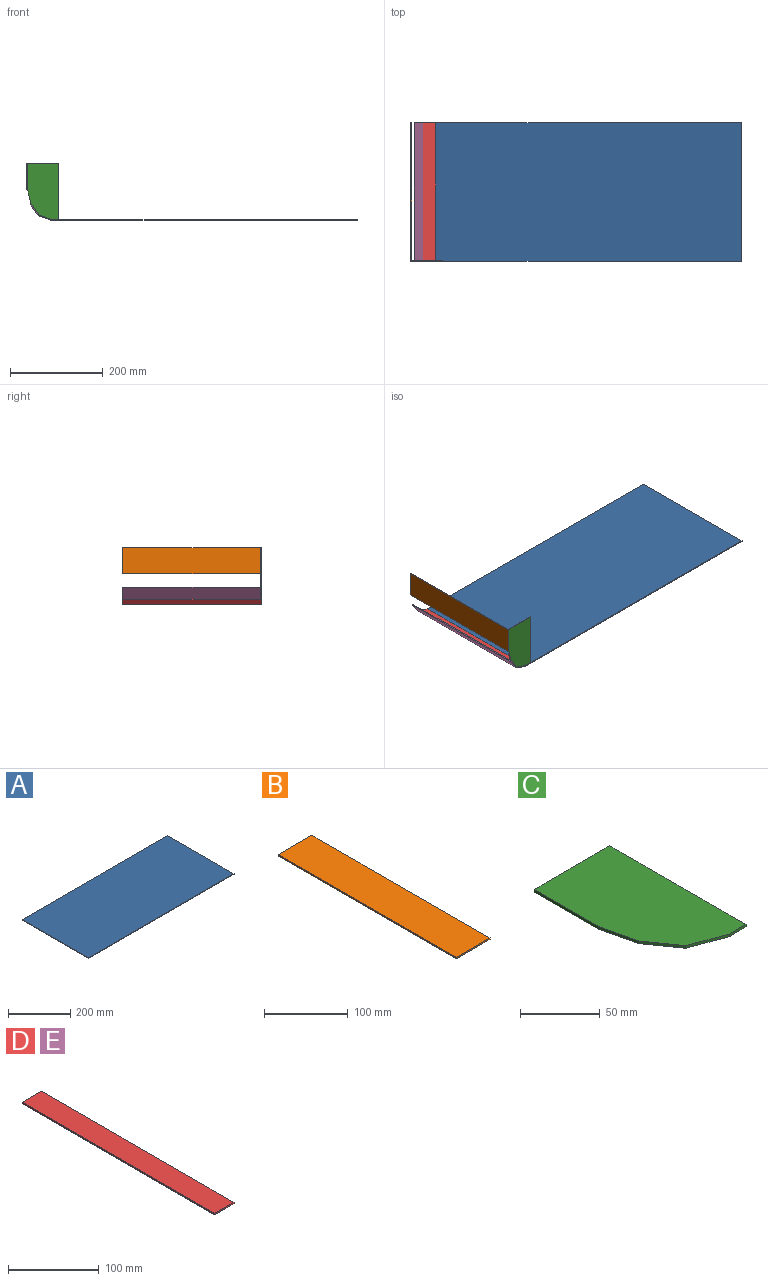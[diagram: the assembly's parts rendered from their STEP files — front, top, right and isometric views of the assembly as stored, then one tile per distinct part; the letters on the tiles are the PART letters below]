
ASSEMBLY  parts=5 mates=4
PART A: 6 faces, bbox 660x300x2 mm
  f0: plane 660x2mm, normal (0,1,0), area 1320mm2, adj f1,f3,f4,f5
  f1: plane 300x2mm, normal (-1,0,0), area 600mm2, adj f0,f2,f4,f5
  f2: plane 660x2mm, normal (0,-1,0), area 1320mm2, adj f1,f3,f4,f5
  f3: plane 300x2mm, normal (1,0,0), area 600mm2, adj f0,f2,f4,f5
  f4: plane 660x300mm, normal (0,0,-1), area 198000mm2, adj f0,f1,f2,f3
  f5: plane 660x300mm, normal (0,0,1), area 198000mm2, adj f0,f1,f2,f3
PART B: 6 faces, bbox 57x300x2 mm
  f0: plane 300x2mm, normal (-1,0,0), area 600mm2, adj f1,f3,f4,f5
  f1: plane 57x2mm, normal (0,-1,0), area 114mm2, adj f0,f2,f4,f5
  f2: plane 300x2mm, normal (1,0,0), area 600mm2, adj f1,f3,f4,f5
  f3: plane 57x2mm, normal (0,1,0), area 114mm2, adj f0,f2,f4,f5
  f4: plane 300x57mm, normal (0,0,-1), area 17100mm2, adj f0,f1,f2,f3
  f5: plane 300x57mm, normal (0,0,1), area 17100mm2, adj f0,f1,f2,f3
PART C: 9 faces, bbox 67.4x121x2 mm
  f0: plane 15x2mm, normal (0,-1,0), area 30mm2, adj f1,f6,f7,f8
  f1: plane 121x2mm, normal (1,0,0), area 242mm2, adj f0,f2,f7,f8
  f2: plane 67.43x2mm, normal (0,1,0), area 134.9mm2, adj f1,f3,f7,f8
  f3: plane 57x2mm, normal (-1,0,0), area 114mm2, adj f2,f4,f7,f8
  f4: plane 29.17x7.03mm, normal (-0.97,-0.23,0), area 60mm2, adj f3,f5,f7,f8
  f5: plane 24.57x17.21mm, normal (-0.82,-0.57,0), area 60mm2, adj f4,f6,f7,f8
  f6: plane 28.19x10.26mm, normal (-0.34,-0.94,0), area 60mm2, adj f0,f5,f7,f8
  f7: plane 121x67.43mm, normal (0,0,-1), area 7278.7mm2, adj f0,f1,f2,f3,f4,f5,f6
  f8: plane 121x67.43mm, normal (0,0,1), area 7278.7mm2, adj f0,f1,f2,f3,f4,f5,f6
PART D: 6 faces, bbox 30x300x2 mm
  f0: plane 300x2mm, normal (-1,0,0), area 600mm2, adj f1,f3,f4,f5
  f1: plane 30x2mm, normal (0,-1,0), area 60mm2, adj f0,f2,f4,f5
  f2: plane 300x2mm, normal (1,0,0), area 600mm2, adj f1,f3,f4,f5
  f3: plane 30x2mm, normal (0,1,0), area 60mm2, adj f0,f2,f4,f5
  f4: plane 300x30mm, normal (0,0,-1), area 9000mm2, adj f0,f1,f2,f3
  f5: plane 300x30mm, normal (0,0,1), area 9000mm2, adj f0,f1,f2,f3
PART E: same geometry as D
PLACE A t=(61.02,-35.41,67.4)mm
PLACE B rot(axis=(0,1,0),90deg) t=(-364.85,-38.41,862.65)mm
PLACE C rot(axis=(1,0,0),90deg) t=(-1503.43,-161.77,19.29)mm
PLACE D rot(axis=(0,1,0),20deg) t=(-736.23,-31.64,221.65)mm
PLACE E rot(axis=(0,1,0),55deg) t=(-599.3,-31.64,447.1)mm
MATE fastened D.f5 <-> C.f6  axis (0.34,0,0.94) through (-340.62,-161.77,77.66)mm
MATE fastened E.f5 <-> C.f5  axis (0.82,0,0.57) through (-357.82,-161.77,102.24)mm
MATE fastened B.f5 <-> C.f3  axis (1,0,0) through (-364.85,-161.77,188.4)mm
MATE fastened A.f5 <-> C.f0  axis (0,0,1) through (-312.43,-161.77,67.4)mm
